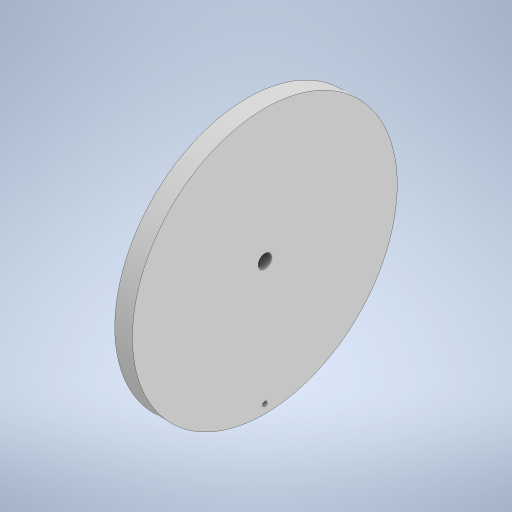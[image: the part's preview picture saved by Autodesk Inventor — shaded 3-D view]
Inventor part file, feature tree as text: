
AUTODESK INVENTOR PART (.ipt)
format: ipt  version: 2023.2 (Build 272271000, 271)  size: 254,976 bytes
history: native  units: mm
features: sketch x2
ambient origin geometry x8: Origin, YZ Plane, XZ Plane, XY Plane, X Axis, Y Axis, Z Axis, Center Point
bodies: Body1 (feature_tree)
feature tree (2):
  sketch  "Sketch1"  dims[d228=60.0mm]
  sketch  "Sketch2"  dims[d229=4.0mm d230=0.0mm d231=3.0mm d232=6.0mm d233=4.0mm d234=2.0mm d235=90.0deg d236=8.0mm d237=20.594885mm d238=1.0mm d239=28.0mm d240=1.0mm d241=6.0mm d242=4.0mm d243=2.0mm d244=90.0deg d245=8.0mm d246=20.594885mm d9=0.5mm d10=0.872665mm d11=0.5mm d12=0.872665mm d13=0.5mm d14=0.872665mm d27=0.5mm d28=0.872665mm d29=0.5mm d30=0.872665mm d88=0.5mm d89=0.872665mm d90=0.5mm d91=0.872665mm d116=0.5mm d117=0.872665mm d118=0.5mm d119=0.872665mm d154=0.5mm d155=0.872665mm d156=0.5mm d157=0.872665mm d181=0.5mm d182=0.872665mm d183=0.5mm d184=0.872665mm d221=0.5mm d222=0.872665mm d223=0.5mm d224=0.872665mm]
